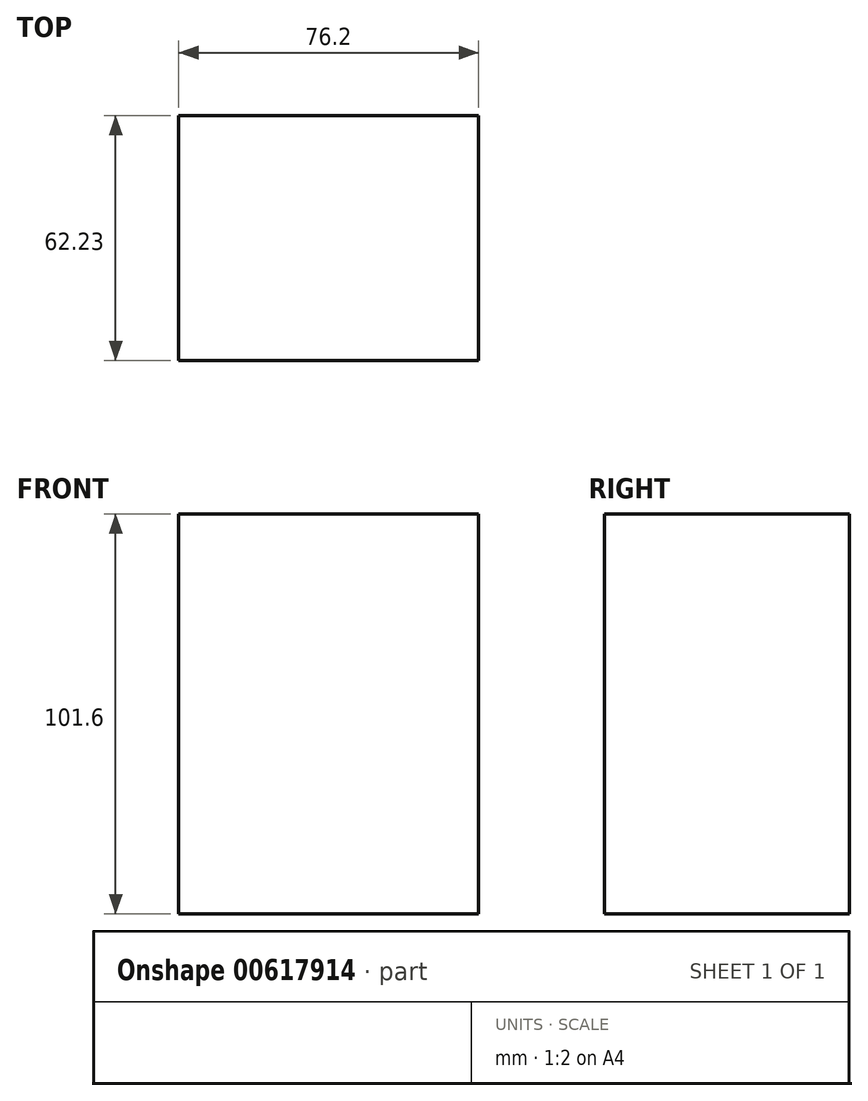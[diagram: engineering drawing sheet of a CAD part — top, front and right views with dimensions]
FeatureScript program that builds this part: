
annotation { "Feature Type Name" : "Feature", "Feature Type Description" : "" }
export const myFeature = defineFeature(function(context is Context, id is Id, definition is map)
    precondition{}
    {
        {
            var Q0;
            Q0=qCreatedBy(makeId("Front.planeOp"),FACE);
            var sketch = newSketch(context, id + "F0", { "sketchPlane" : qUnion([Q0])});
            skLineSegment(sketch, "E0", {"start": v(0, 0) * mm, "end": v(76.2, 0) * mm});
            skLineSegment(sketch, "E1", {"start": v(76.2, 0) * mm, "end": v(76.2, 101.6) * mm});
            skLineSegment(sketch, "E2", {"start": v(76.2, 101.6) * mm, "end": v(0, 101.6) * mm});
            skLineSegment(sketch, "E3", {"start": v(0, 101.6) * mm, "end": v(0, 0) * mm});
            skArc(sketch, "E4", {"start": v(76.2, 101.6) * mm, "mid": v(38.1, 139.7) * mm, "end": v(0, 101.6) * mm});
            skSolve(sketch);
        }
        {
            var Q0;
            Q0=makeQuery(id+"F0.imprint","IMPRINT",FACE,{"disambiguationData":[TD([[makeQuery(id+"F0.imprint","IMPRINT",EDGE,{"derivedFrom":sQuery(id+"F0.wireOp",EDGE,"E0")}),1.0]])]});
            extrude(context, id + "F1", {"entities" : qUnion([Q0]), "depth" : 62.23 * mm, "offsetDistance" : 25.4 * mm});
        }
    });
